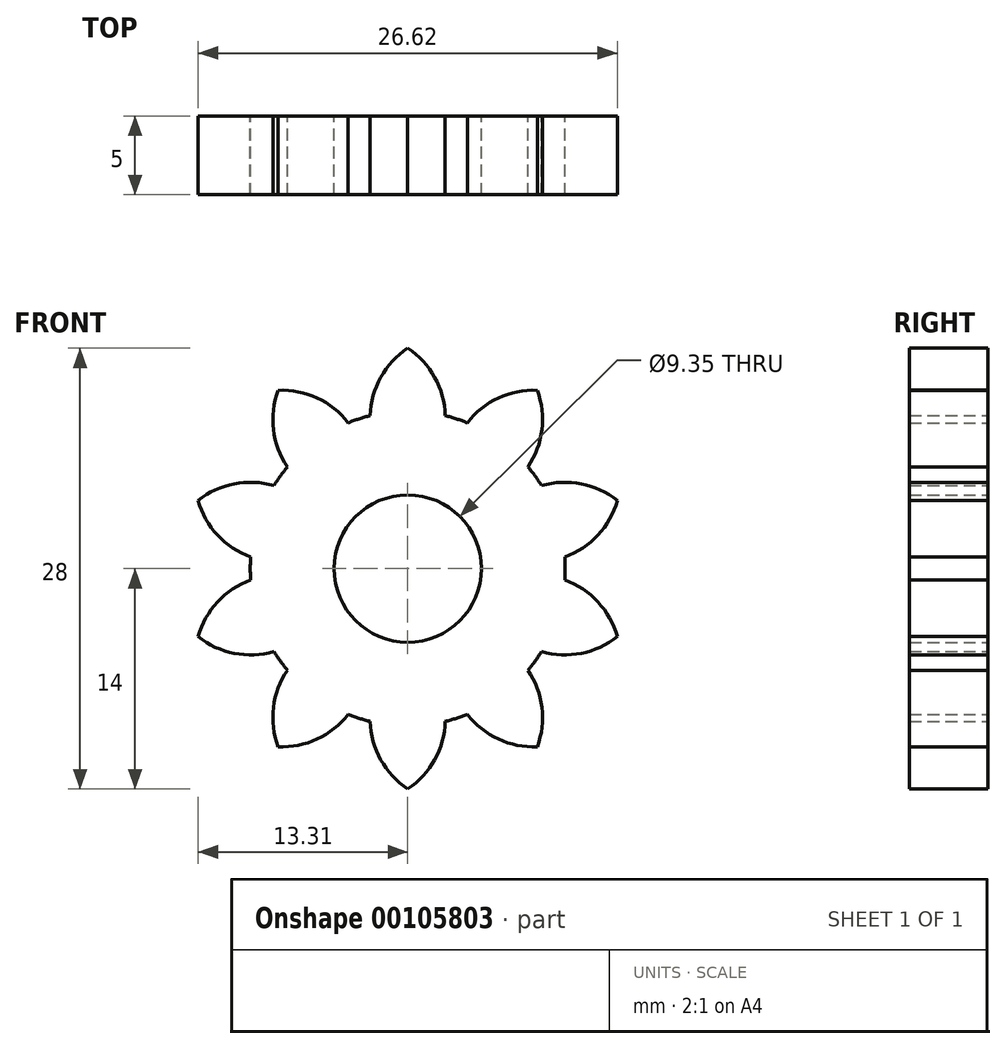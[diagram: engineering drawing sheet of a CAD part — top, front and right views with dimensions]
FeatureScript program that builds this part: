
annotation { "Feature Type Name" : "Feature", "Feature Type Description" : "" }
export const myFeature = defineFeature(function(context is Context, id is Id, definition is map)
    precondition{}
    {
        {
            var Q0;
            Q0=qCreatedBy(makeId("Front.planeOp"),FACE);
            var sketch = newSketch(context, id + "F0", { "sketchPlane" : qUnion([Q0])});
            skCircle(sketch, "E0", {"center": v(0, 0) * mm, "radius": 10 * mm});
            skArc(sketch, "E1", {"start": v(0, 14) * mm, "mid": v(-1.71, 12.15) * mm, "end": v(-2.38, 9.71) * mm});
            skArc(sketch, "E2.MirrorCS", {"start": v(0, 14) * mm, "mid": v(1.71, 12.15) * mm, "end": v(2.38, 9.71) * mm});
            skArc(sketch, "E3.1.0", {"start": v(-8.23, 11.32) * mm, "mid": v(-8.53, 8.82) * mm, "end": v(-7.64, 6.46) * mm});
            skArc(sketch, "E3.1.1", {"start": v(-8.23, 11.32) * mm, "mid": v(-5.75, 10.83) * mm, "end": v(-3.78, 9.26) * mm});
            skArc(sketch, "E3.2.0", {"start": v(-13.31, 4.33) * mm, "mid": v(-12.08, 2.12) * mm, "end": v(-9.97, 0.74) * mm});
            skArc(sketch, "E3.2.1", {"start": v(-13.31, 4.33) * mm, "mid": v(-11.02, 5.38) * mm, "end": v(-8.5, 5.27) * mm});
            skArc(sketch, "E3.3.0", {"start": v(-13.31, -4.33) * mm, "mid": v(-11.02, -5.38) * mm, "end": v(-8.5, -5.27) * mm});
            skArc(sketch, "E3.3.1", {"start": v(-13.31, -4.33) * mm, "mid": v(-12.08, -2.12) * mm, "end": v(-9.97, -0.74) * mm});
            skArc(sketch, "E3.4.0", {"start": v(-8.23, -11.32) * mm, "mid": v(-5.75, -10.83) * mm, "end": v(-3.78, -9.26) * mm});
            skArc(sketch, "E3.4.1", {"start": v(-8.23, -11.32) * mm, "mid": v(-8.53, -8.82) * mm, "end": v(-7.64, -6.46) * mm});
            skArc(sketch, "E3.5.0", {"start": v(0, -14) * mm, "mid": v(1.71, -12.15) * mm, "end": v(2.38, -9.71) * mm});
            skArc(sketch, "E3.5.1", {"start": v(0, -14) * mm, "mid": v(-1.71, -12.15) * mm, "end": v(-2.38, -9.71) * mm});
            skArc(sketch, "E3.6.0", {"start": v(8.23, -11.32) * mm, "mid": v(8.53, -8.82) * mm, "end": v(7.64, -6.46) * mm});
            skArc(sketch, "E3.6.1", {"start": v(8.23, -11.32) * mm, "mid": v(5.75, -10.83) * mm, "end": v(3.78, -9.26) * mm});
            skArc(sketch, "E3.7.0", {"start": v(13.31, -4.33) * mm, "mid": v(12.08, -2.12) * mm, "end": v(9.97, -0.74) * mm});
            skArc(sketch, "E3.7.1", {"start": v(13.31, -4.33) * mm, "mid": v(11.02, -5.38) * mm, "end": v(8.5, -5.27) * mm});
            skArc(sketch, "E3.8.0", {"start": v(13.31, 4.33) * mm, "mid": v(11.02, 5.38) * mm, "end": v(8.5, 5.27) * mm});
            skArc(sketch, "E3.8.1", {"start": v(13.31, 4.33) * mm, "mid": v(12.08, 2.12) * mm, "end": v(9.97, 0.74) * mm});
            skArc(sketch, "E3.9.0", {"start": v(8.23, 11.32) * mm, "mid": v(5.75, 10.83) * mm, "end": v(3.78, 9.26) * mm});
            skArc(sketch, "E3.9.1", {"start": v(8.23, 11.32) * mm, "mid": v(8.53, 8.82) * mm, "end": v(7.64, 6.46) * mm});
            skCircle(sketch, "E4", {"center": v(0, 0) * mm, "radius": 4.68 * mm});
            skSolve(sketch);
        }
        {
            var Q0;
            {var subQ0=sQuery(id+"F0.wireOp",EDGE,"E3.8.0");Q0=makeQuery(id+"F0.imprint","IMPRINT",FACE,{"disambiguationData":[TD([[makeQuery(id+"F0.imprint","IMPRINT",EDGE,{"derivedFrom":subQ0}),1.0]])]});}
            var Q1;
            {var subQ0=sQuery(id+"F0.wireOp",EDGE,"E3.9.0");Q1=makeQuery(id+"F0.imprint","IMPRINT",FACE,{"disambiguationData":[TD([[makeQuery(id+"F0.imprint","IMPRINT",EDGE,{"derivedFrom":subQ0}),1.0]])]});}
            var Q2;
            {var subQ0=sQuery(id+"F0.wireOp",EDGE,"E1");Q2=makeQuery(id+"F0.imprint","IMPRINT",FACE,{"disambiguationData":[TD([[makeQuery(id+"F0.imprint","IMPRINT",EDGE,{"derivedFrom":subQ0}),1.0]])]});}
            var Q3;
            {var subQ0=sQuery(id+"F0.wireOp",EDGE,"E3.1.0");Q3=makeQuery(id+"F0.imprint","IMPRINT",FACE,{"disambiguationData":[TD([[makeQuery(id+"F0.imprint","IMPRINT",EDGE,{"derivedFrom":subQ0}),1.0]])]});}
            var Q4;
            {var subQ0=sQuery(id+"F0.wireOp",EDGE,"E3.2.0");Q4=makeQuery(id+"F0.imprint","IMPRINT",FACE,{"disambiguationData":[TD([[makeQuery(id+"F0.imprint","IMPRINT",EDGE,{"derivedFrom":subQ0}),1.0]])]});}
            var Q5;
            {var subQ0=sQuery(id+"F0.wireOp",EDGE,"E3.3.0");Q5=makeQuery(id+"F0.imprint","IMPRINT",FACE,{"disambiguationData":[TD([[makeQuery(id+"F0.imprint","IMPRINT",EDGE,{"derivedFrom":subQ0}),1.0]])]});}
            var Q6;
            {var subQ0=sQuery(id+"F0.wireOp",EDGE,"E3.4.0");Q6=makeQuery(id+"F0.imprint","IMPRINT",FACE,{"disambiguationData":[TD([[makeQuery(id+"F0.imprint","IMPRINT",EDGE,{"derivedFrom":subQ0}),1.0]])]});}
            var Q7;
            {var subQ0=sQuery(id+"F0.wireOp",EDGE,"E3.5.0");Q7=makeQuery(id+"F0.imprint","IMPRINT",FACE,{"disambiguationData":[TD([[makeQuery(id+"F0.imprint","IMPRINT",EDGE,{"derivedFrom":subQ0}),1.0]])]});}
            var Q8;
            {var subQ0=sQuery(id+"F0.wireOp",EDGE,"E3.6.0");Q8=makeQuery(id+"F0.imprint","IMPRINT",FACE,{"disambiguationData":[TD([[makeQuery(id+"F0.imprint","IMPRINT",EDGE,{"derivedFrom":subQ0}),1.0]])]});}
            var Q9;
            {var subQ0=sQuery(id+"F0.wireOp",EDGE,"E3.7.0");Q9=makeQuery(id+"F0.imprint","IMPRINT",FACE,{"disambiguationData":[TD([[makeQuery(id+"F0.imprint","IMPRINT",EDGE,{"derivedFrom":subQ0}),1.0]])]});}
            var Q10;
            Q10=makeQuery(id+"F0.imprint","IMPRINT",FACE,{"disambiguationData":[TD([[makeQuery(id+"F0.imprint","IMPRINT",EDGE,{"derivedFrom":sQuery(id+"F0.wireOp",EDGE,"E4")}),-1.0]])]});
            extrude(context, id + "F1", {"entities" : qUnion([Q0, Q1, Q2, Q3, Q4, Q5, Q6, Q7, Q8, Q9, Q10]), "depth" : 5 * mm});
        }
    });
